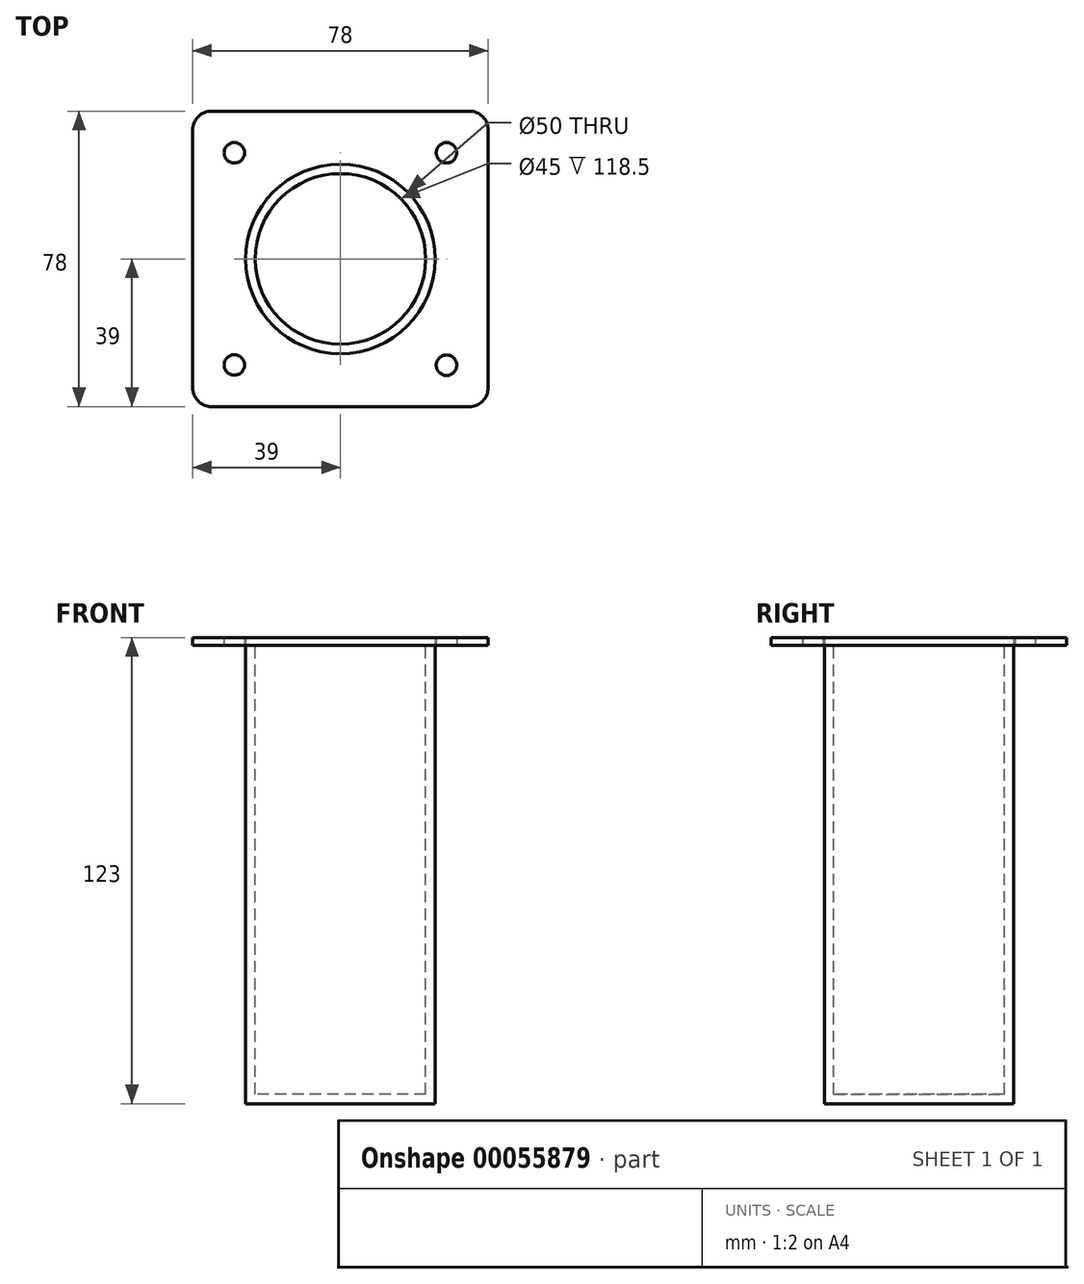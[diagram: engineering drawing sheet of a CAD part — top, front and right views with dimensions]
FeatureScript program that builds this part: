
annotation { "Feature Type Name" : "Feature", "Feature Type Description" : "" }
export const myFeature = defineFeature(function(context is Context, id is Id, definition is map)
    precondition{}
    {
        {
            var Q0;
            Q0=qCreatedBy(makeId("Top.planeOp"),FACE);
            var sketch = newSketch(context, id + "F0", { "sketchPlane" : qUnion([Q0])});
            skCircle(sketch, "E0", {"center": v(0, 0) * mm, "radius": 25 * mm});
            skSolve(sketch);
        }
        {
            var Q0;
            Q0=makeQuery(id+"F0.imprint","IMPRINT",FACE,{"disambiguationData":[TD([[makeQuery(id+"F0.imprint","IMPRINT",EDGE,{"derivedFrom":sQuery(id+"F0.wireOp",EDGE,"E0")}),1.0]])]});
            extrude(context, id + "F1", {"entities" : qUnion([Q0]), "oppositeDirection" : true, "depth" : 121 * mm});
        }
        {
            var Q0;
            Q0=makeQuery(id+"F1.opExtrude","CAP_FACE",FACE,{"disambiguationData":[OSD([sQuery(id+"F0.wireOp",EDGE,"E0")])],"isStart":true});
            shell(context, id + "F2", {"entities" : qUnion([Q0]), "thickness" : 2.5 * mm});
        }
        {
            var Q0;
            Q0=makeQuery(id+"F1.opExtrude","CAP_FACE",FACE,{"disambiguationData":[OSD([sQuery(id+"F0.wireOp",EDGE,"E0")])],"isStart":true});
            var sketch = newSketch(context, id + "F3", { "sketchPlane" : qUnion([Q0])});
            skLineSegment(sketch, "E1.rect.bottom", {"start": v(34, -39) * mm, "end": v(-34, -39) * mm});
            skLineSegment(sketch, "E1.rect.top", {"start": v(34, 39) * mm, "end": v(-34, 39) * mm});
            skLineSegment(sketch, "E1.rect.left", {"start": v(39, -34) * mm, "end": v(39, 34) * mm});
            skLineSegment(sketch, "E1.rect.right", {"start": v(-39, -34) * mm, "end": v(-39, 34) * mm});
            skPoint(sketch, "E1.rect.middle", {"position": v(0, 0) * mm});
            skLineSegment(sketch, "E2", {"start": v(-39, 28) * mm, "end": v(41.6, 28) * mm, "construction": true});
            skLineSegment(sketch, "E3", {"start": v(-39, -28) * mm, "end": v(39, -28) * mm, "construction": true});
            skLineSegment(sketch, "E4", {"start": v(-28, 39) * mm, "end": v(-28, -39) * mm, "construction": true});
            skLineSegment(sketch, "E5", {"start": v(28, 39) * mm, "end": v(28, -39) * mm, "construction": true});
            skCircle(sketch, "E6", {"center": v(-28, 28) * mm, "radius": 2.7 * mm});
            skCircle(sketch, "E7", {"center": v(28, 28) * mm, "radius": 2.7 * mm});
            skCircle(sketch, "E8", {"center": v(-28, -28) * mm, "radius": 2.7 * mm});
            skCircle(sketch, "E9", {"center": v(28, -28.07) * mm, "radius": 2.7 * mm});
            skPoint(sketch, "E10.visualSharp", {"position": v(-39, 39) * mm});
            skArc(sketch, "E10.filletArc", {"start": v(-34, 39) * mm, "mid": v(-37.54, 37.54) * mm, "end": v(-39, 34) * mm});
            skPoint(sketch, "E11.visualSharp", {"position": v(39, 39) * mm});
            skArc(sketch, "E11.filletArc", {"start": v(39, 34) * mm, "mid": v(37.54, 37.54) * mm, "end": v(34, 39) * mm});
            skPoint(sketch, "E12.visualSharp", {"position": v(-39, -39) * mm});
            skArc(sketch, "E12.filletArc", {"start": v(-39, -34) * mm, "mid": v(-37.54, -37.54) * mm, "end": v(-34, -39) * mm});
            skPoint(sketch, "E13.visualSharp", {"position": v(39, -39) * mm});
            skArc(sketch, "E13.filletArc", {"start": v(34, -39) * mm, "mid": v(37.54, -37.54) * mm, "end": v(39, -34) * mm});
            skSolve(sketch);
        }
        {
            var Q0;
            Q0=makeQuery(id+"F3.imprint","IMPRINT",FACE,{"disambiguationData":[TD([[makeQuery(id+"F3.imprint","IMPRINT",EDGE,{"derivedFrom":sQuery(id+"F3.wireOp",EDGE,"E1.rect.bottom")}),-1.0]])]});
            extrude(context, id + "F4", {"entities" : qUnion([Q0]), "depth" : 2 * mm});
        }
    });
